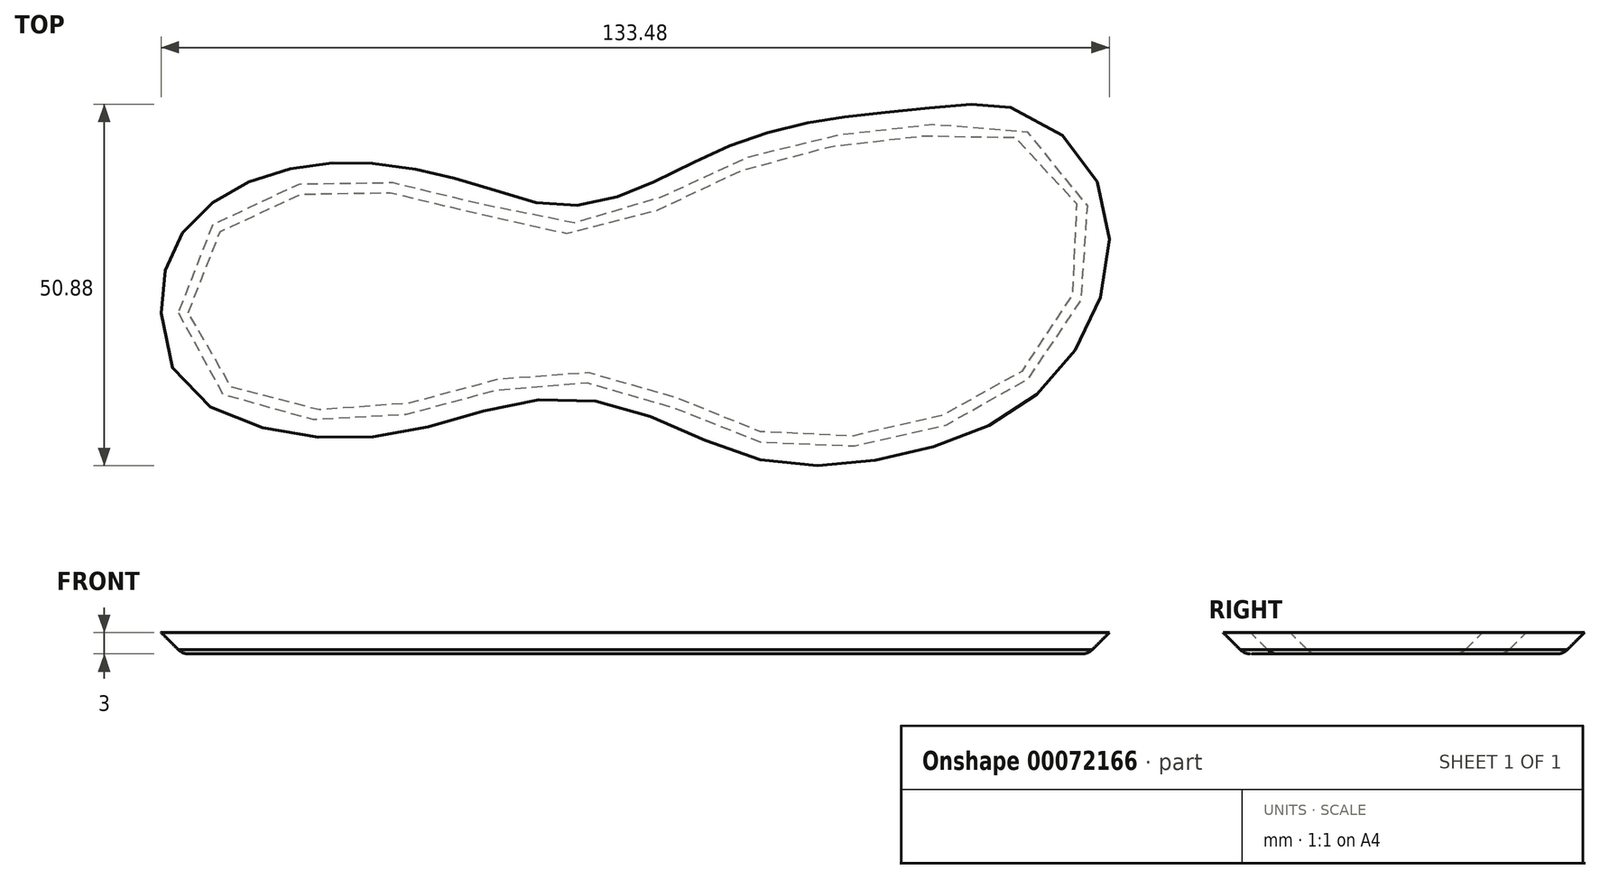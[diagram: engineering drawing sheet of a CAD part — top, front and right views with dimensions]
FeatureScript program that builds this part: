
annotation { "Feature Type Name" : "Feature", "Feature Type Description" : "" }
export const myFeature = defineFeature(function(context is Context, id is Id, definition is map)
    precondition{}
    {
        {
            var Q0;
            Q0=qCreatedBy(makeId("Top.planeOp"),FACE);
            var sketch = newSketch(context, id + "F0", { "sketchPlane" : qUnion([Q0])});
            skFitSpline(sketch, "E0", {"points": [v(-69.21, 0) * mm, v(-67.16, 10.41) * mm, v(-58.07, 19.21) * mm, v(-40.47, 23.32) * mm, v(-24.34, 20.68) * mm, v(-17.6, 18.62) * mm, v(-9.97, 17.16) * mm, v(0, 19.8) * mm, v(11.15, 25.08) * mm, v(23.76, 28.89) * mm, v(40.48, 30.94) * mm, v(53.97, 30.65) * mm, v(65.41, 21.26) * mm, v(67.76, 5.13) * mm, v(57.79, -12.47) * mm, v(37.55, -21.85) * mm, v(16.43, -22.44) * mm, v(0, -15.98) * mm, v(-11.43, -13.93) * mm, v(-21.4, -15.7) * mm, v(-40.76, -19.5) * mm, v(-64.52, -12.47) * mm, v(-69.21, 0) * mm]});
            skSolve(sketch);
        }
        {
            var Q0;
            Q0 = qSketchRegion(id + "F0", true);
            extrude(context, id + "F1", {"entities" : qUnion([Q0]), "depth" : 3 * mm});
        }
        {
            var Q0;
            Q0=makeQuery(id+"F1.opExtrude","CAP_FACE",FACE,{"disambiguationData":[OSD([sQuery(id+"F0.wireOp",EDGE,"E0")])],"isStart":true});
            chamfer(context, id + "F2", {"entities" : qUnion([Q0]), "chamferType" : ChamferType.TWO_OFFSETS, "width1" : 5 * mm, "oppositeDirection" : false, "width2" : 5 * mm, "tangentPropagation" : true});
        }
        {
            var Q0;
            {var subQ0=sQuery(id+"F0.wireOp",EDGE,"E0");Q0=makeQuery(id+"F2.opChamfer","BLEND_EDGE",EDGE,{"blendedFrom":[makeQuery(id+"F1.opExtrude","CAP_EDGE",EDGE,{"disambiguationData":[OSD([subQ0])],"isStart":true}),makeQuery(id+"F1.opExtrude","CAP_FACE",FACE,{"disambiguationData":[OSD([subQ0])],"isStart":true})],"blendedInto":[makeQuery(id+"F1.opExtrude","CAP_FACE",FACE,{"disambiguationData":[OSD([subQ0])],"isStart":true})]});}
            fillet(context, id + "F3", {"entities" : qUnion([Q0]), "radius" : 2 * mm, "tangentPropagation" : true, "allowEdgeOverflow" : false});
        }
    });
